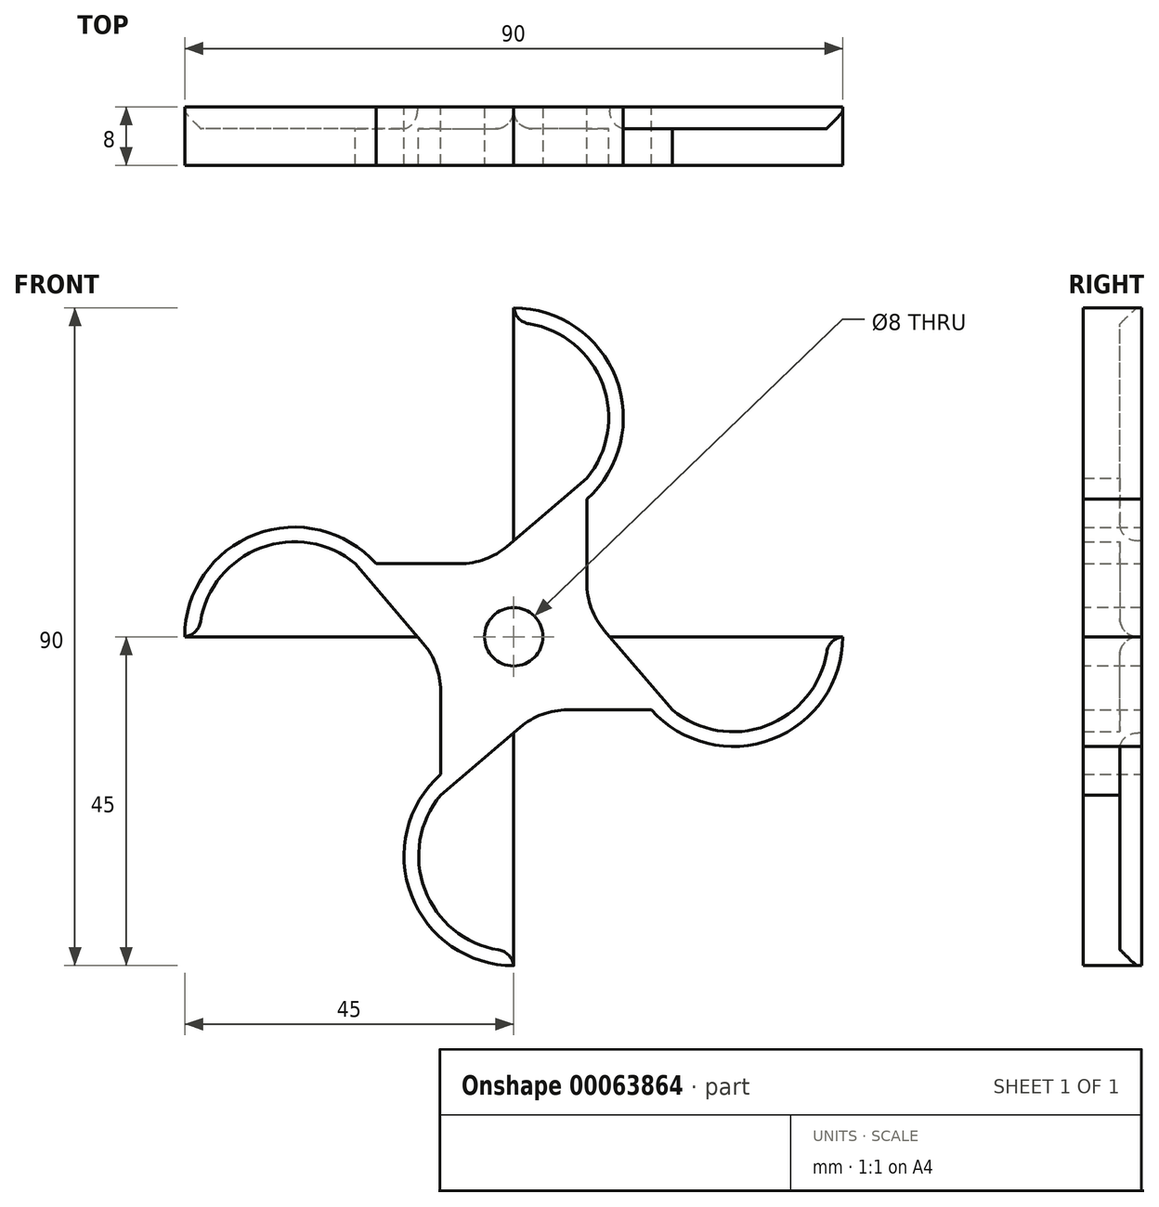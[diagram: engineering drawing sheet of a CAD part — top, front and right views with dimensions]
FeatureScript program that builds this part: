
annotation { "Feature Type Name" : "Feature", "Feature Type Description" : "" }
export const myFeature = defineFeature(function(context is Context, id is Id, definition is map)
    precondition{}
    {
        {
            var Q0;
            Q0=qCreatedBy(makeId("Front.planeOp"),FACE);
            var sketch = newSketch(context, id + "F0", { "sketchPlane" : qUnion([Q0])});
            skArc(sketch, "E0", {"start": v(10, 18.82) * mm, "mid": v(14.01, 35.35) * mm, "end": v(0, 45) * mm});
            skArc(sketch, "E1", {"start": v(10, 21.7) * mm, "mid": v(11.77, 35.52) * mm, "end": v(0, 43) * mm});
            skLineSegment(sketch, "E2", {"start": v(0, 13.15) * mm, "end": v(0, 10) * mm});
            skLineSegment(sketch, "E3", {"start": v(10, 7.38) * mm, "end": v(10, 18.82) * mm});
            skLineSegment(sketch, "E4", {"start": v(0, 43) * mm, "end": v(0, 45) * mm});
            skArc(sketch, "E5.1.1", {"start": v(-21.7, 10) * mm, "mid": v(-35.52, 11.77) * mm, "end": v(-43, 0) * mm});
            skLineSegment(sketch, "E5.1.2", {"start": v(-43, 0) * mm, "end": v(-45, 0) * mm});
            skArc(sketch, "E5.1.3", {"start": v(-18.82, 10) * mm, "mid": v(-35.35, 14.01) * mm, "end": v(-45, 0) * mm});
            skLineSegment(sketch, "E5.1.4", {"start": v(-7.38, 10) * mm, "end": v(-18.82, 10) * mm});
            skArc(sketch, "E5.2.1", {"start": v(-10, -21.7) * mm, "mid": v(-11.77, -35.52) * mm, "end": v(0, -43) * mm});
            skLineSegment(sketch, "E5.2.2", {"start": v(0, -43) * mm, "end": v(0, -45) * mm});
            skArc(sketch, "E5.2.3", {"start": v(-10, -18.82) * mm, "mid": v(-14.01, -35.35) * mm, "end": v(0, -45) * mm});
            skLineSegment(sketch, "E5.2.4", {"start": v(-10, -7.38) * mm, "end": v(-10, -18.82) * mm});
            skLineSegment(sketch, "E5.3.0", {"start": v(17, 0) * mm, "end": v(17, 0) * mm});
            skArc(sketch, "E5.3.1", {"start": v(21.7, -10) * mm, "mid": v(35.52, -11.77) * mm, "end": v(43, 0) * mm});
            skLineSegment(sketch, "E5.3.2", {"start": v(43, 0) * mm, "end": v(45, 0) * mm});
            skArc(sketch, "E5.3.3", {"start": v(18.82, -10) * mm, "mid": v(35.35, -14.01) * mm, "end": v(45, 0) * mm});
            skLineSegment(sketch, "E5.3.4", {"start": v(7.38, -10) * mm, "end": v(18.82, -10) * mm});
            skPoint(sketch, "E5.center", {"position": v(0, 0) * mm});
            skPoint(sketch, "E6.visualSharp", {"position": v(10, 0) * mm});
            skLineSegment(sketch, "E7", {"start": v(10, 21.7) * mm, "end": v(-0.88, 12.4) * mm});
            skPoint(sketch, "E8.orphan", {"position": v(0, 17) * mm});
            skPoint(sketch, "E9.newPointB", {"position": v(0, 10) * mm});
            skArc(sketch, "E9.filletArc", {"start": v(-7.38, 10) * mm, "mid": v(-3.92, 10.62) * mm, "end": v(-0.88, 12.4) * mm});
            skArc(sketch, "E10.1.0", {"start": v(-10, -7.38) * mm, "mid": v(-10.62, -3.92) * mm, "end": v(-12.4, -0.88) * mm});
            skLineSegment(sketch, "E10.1.1", {"start": v(-21.7, 10) * mm, "end": v(-12.4, -0.88) * mm});
            skArc(sketch, "E10.2.0", {"start": v(7.38, -10) * mm, "mid": v(3.92, -10.62) * mm, "end": v(0.88, -12.4) * mm});
            skLineSegment(sketch, "E10.2.1", {"start": v(-10, -21.7) * mm, "end": v(0.88, -12.4) * mm});
            skArc(sketch, "E10.3.0", {"start": v(10, 7.38) * mm, "mid": v(10.62, 3.92) * mm, "end": v(12.4, 0.88) * mm});
            skLineSegment(sketch, "E10.3.1", {"start": v(21.7, -10) * mm, "end": v(12.4, 0.88) * mm});
            skPoint(sketch, "E11.orphan", {"position": v(17, 0) * mm});
            skPoint(sketch, "E12.orphan", {"position": v(10, 7) * mm});
            skPoint(sketch, "E13.orphan", {"position": v(0, -17) * mm});
            skPoint(sketch, "E14.orphan", {"position": v(0, -10) * mm});
            skPoint(sketch, "E15.orphan", {"position": v(-10, 0) * mm});
            skPoint(sketch, "E16.orphan", {"position": v(-17, 0) * mm});
            skCircle(sketch, "E17", {"center": v(0, 0) * mm, "radius": 3.75 * mm});
            skSolve(sketch);
        }
        {
            var Q0;
            Q0=makeQuery(id+"F0.imprint","IMPRINT",FACE,{"disambiguationData":[TD([[makeQuery(id+"F0.imprint","IMPRINT",EDGE,{"derivedFrom":sQuery(id+"F0.wireOp",EDGE,"E0")}),1.0]])]});
            extrude(context, id + "F1", {"entities" : qUnion([Q0]), "depth" : 5 * mm});
        }
        {
            var Q0;
            Q0=makeQuery(id+"F1.opExtrude","CAP_FACE",FACE,{"disambiguationData":[OSD([sQuery(id+"F0.wireOp",EDGE,"E0"),sQuery(id+"F0.wireOp",EDGE,"E1"),sQuery(id+"F0.wireOp",EDGE,"E3"),sQuery(id+"F0.wireOp",EDGE,"E4"),sQuery(id+"F0.wireOp",EDGE,"E5.1.1"),sQuery(id+"F0.wireOp",EDGE,"E5.1.2"),sQuery(id+"F0.wireOp",EDGE,"E5.1.3"),sQuery(id+"F0.wireOp",EDGE,"E5.1.4"),sQuery(id+"F0.wireOp",EDGE,"E5.2.1"),sQuery(id+"F0.wireOp",EDGE,"E5.2.2"),sQuery(id+"F0.wireOp",EDGE,"E5.2.3"),sQuery(id+"F0.wireOp",EDGE,"E5.2.4"),sQuery(id+"F0.wireOp",EDGE,"E5.3.1"),sQuery(id+"F0.wireOp",EDGE,"E5.3.2"),sQuery(id+"F0.wireOp",EDGE,"E5.3.3"),sQuery(id+"F0.wireOp",EDGE,"E5.3.4"),sQuery(id+"F0.wireOp",EDGE,"E7"),sQuery(id+"F0.wireOp",EDGE,"E9.filletArc"),sQuery(id+"F0.wireOp",EDGE,"E10.1.0"),sQuery(id+"F0.wireOp",EDGE,"E10.1.1"),sQuery(id+"F0.wireOp",EDGE,"E10.2.0"),sQuery(id+"F0.wireOp",EDGE,"E10.2.1"),sQuery(id+"F0.wireOp",EDGE,"E10.3.0"),sQuery(id+"F0.wireOp",EDGE,"E10.3.1"),sQuery(id+"F0.wireOp",EDGE,"E17")])],"isStart":true});
            var sketch = newSketch(context, id + "F2", { "sketchPlane" : qUnion([Q0])});
            skArc(sketch, "E18", {"start": v(0, 45) * mm, "mid": v(-14.01, 35.35) * mm, "end": v(-10, 18.82) * mm});
            skPoint(sketch, "E18.first.point", {"position": v(-2.98, 44.7) * mm});
            skPoint(sketch, "E18.second.point", {"position": v(-12.28, 38.61) * mm});
            skPoint(sketch, "E18.third.point", {"position": v(-10.97, 19.77) * mm});
            skLineSegment(sketch, "E19", {"start": v(0, 9.88) * mm, "end": v(0, 45) * mm});
            skLineSegment(sketch, "E20", {"start": v(-10, 18.82) * mm, "end": v(-10, 7.38) * mm});
            skArc(sketch, "E21", {"start": v(-12.4, 0.88) * mm, "mid": v(-10.62, 3.92) * mm, "end": v(-10, 7.38) * mm});
            skPoint(sketch, "E21.first.point", {"position": v(-11.49, 2.13) * mm});
            skPoint(sketch, "E21.second.point", {"position": v(-11, 3.02) * mm});
            skPoint(sketch, "E21.third.point", {"position": v(-10.2, 5.4) * mm});
            skLineSegment(sketch, "E22", {"start": v(-13.15, 0) * mm, "end": v(-12.4, 0.88) * mm});
            skLineSegment(sketch, "E23", {"start": v(-13.15, 0) * mm, "end": v(-3.75, 0) * mm});
            skLineSegment(sketch, "E24", {"start": v(0, 3.75) * mm, "end": v(0, 9.88) * mm});
            skArc(sketch, "E25", {"start": v(0, 3.75) * mm, "mid": v(-2.65, 2.65) * mm, "end": v(-3.75, 0) * mm});
            skPoint(sketch, "E25.third.point", {"position": v(-2.3, 2.96) * mm});
            skArc(sketch, "E26.1.0", {"start": v(-3.75, 0) * mm, "mid": v(-2.65, -2.65) * mm, "end": v(0, -3.75) * mm});
            skLineSegment(sketch, "E26.1.1", {"start": v(0, -13.15) * mm, "end": v(-0.88, -12.4) * mm});
            skArc(sketch, "E26.1.2", {"start": v(-0.88, -12.4) * mm, "mid": v(-3.92, -10.62) * mm, "end": v(-7.38, -10) * mm});
            skLineSegment(sketch, "E26.1.3", {"start": v(-18.82, -10) * mm, "end": v(-7.38, -10) * mm});
            skArc(sketch, "E26.1.4", {"start": v(-45, 0) * mm, "mid": v(-35.35, -14.01) * mm, "end": v(-18.82, -10) * mm});
            skLineSegment(sketch, "E26.1.5", {"start": v(-9.88, 0) * mm, "end": v(-45, 0) * mm});
            skLineSegment(sketch, "E26.1.6", {"start": v(-3.75, 0) * mm, "end": v(-9.88, 0) * mm});
            skArc(sketch, "E26.2.0", {"start": v(0, -3.75) * mm, "mid": v(2.65, -2.65) * mm, "end": v(3.75, 0) * mm});
            skLineSegment(sketch, "E26.2.1", {"start": v(13.15, 0) * mm, "end": v(12.4, -0.88) * mm});
            skArc(sketch, "E26.2.2", {"start": v(12.4, -0.88) * mm, "mid": v(10.62, -3.92) * mm, "end": v(10, -7.38) * mm});
            skLineSegment(sketch, "E26.2.3", {"start": v(10, -18.82) * mm, "end": v(10, -7.38) * mm});
            skArc(sketch, "E26.2.4", {"start": v(0, -45) * mm, "mid": v(14.01, -35.35) * mm, "end": v(10, -18.82) * mm});
            skLineSegment(sketch, "E26.2.5", {"start": v(0, -9.88) * mm, "end": v(0, -45) * mm});
            skLineSegment(sketch, "E26.2.6", {"start": v(0, -3.75) * mm, "end": v(0, -9.88) * mm});
            skArc(sketch, "E26.3.0", {"start": v(3.75, 0) * mm, "mid": v(2.65, 2.65) * mm, "end": v(0, 3.75) * mm});
            skLineSegment(sketch, "E26.3.1", {"start": v(0, 13.15) * mm, "end": v(0.88, 12.4) * mm});
            skArc(sketch, "E26.3.2", {"start": v(0.88, 12.4) * mm, "mid": v(3.92, 10.62) * mm, "end": v(7.38, 10) * mm});
            skLineSegment(sketch, "E26.3.3", {"start": v(18.82, 10) * mm, "end": v(7.38, 10) * mm});
            skArc(sketch, "E26.3.4", {"start": v(45, 0) * mm, "mid": v(35.35, 14.01) * mm, "end": v(18.82, 10) * mm});
            skLineSegment(sketch, "E26.3.5", {"start": v(9.88, 0) * mm, "end": v(45, 0) * mm});
            skLineSegment(sketch, "E26.3.6", {"start": v(3.75, 0) * mm, "end": v(9.88, 0) * mm});
            skSolve(sketch);
        }
        {
            var Q0;
            {var subQ1=makeQuery(id+"F1.opExtrude","CAP_EDGE",EDGE,{"disambiguationData":[OSD([sQuery(id+"F0.wireOp",EDGE,"E1")])],"isStart":true});Q0=makeQuery(id+"F2.imprint","IMPRINT",FACE,{"disambiguationData":[TD([[makeQuery(id+"F2.imprint","IMPRINT",EDGE,{"derivedFrom":subQ1}),-1.0]])]});}
            var Q1;
            {var subQ6=sQuery(id+"F2.wireOp",EDGE,"E18");Q1=makeQuery(id+"F2.imprint","IMPRINT",FACE,{"disambiguationData":[TD([[makeQuery(id+"F2.imprint","IMPRINT",EDGE,{"derivedFrom":subQ6}),-1.0]])]});}
            var Q2;
            {var subQ4=sQuery(id+"F2.wireOp",EDGE,"E24");Q2=makeQuery(id+"F2.imprint","IMPRINT",FACE,{"disambiguationData":[TD([[makeQuery(id+"F2.imprint","IMPRINT",EDGE,{"derivedFrom":subQ4}),-1.0]])]});}
            var Q3;
            {var subQ1=makeQuery(id+"F1.opExtrude","CAP_EDGE",EDGE,{"disambiguationData":[OSD([sQuery(id+"F0.wireOp",EDGE,"E5.1.1")])],"isStart":true});Q3=makeQuery(id+"F2.imprint","IMPRINT",FACE,{"disambiguationData":[TD([[makeQuery(id+"F2.imprint","IMPRINT",EDGE,{"derivedFrom":subQ1}),-1.0]])]});}
            var Q4;
            Q4=makeQuery(id+"F2.imprint","IMPRINT",FACE,{"disambiguationData":[TD([[makeQuery(id+"F2.imprint","IMPRINT",EDGE,{"derivedFrom":sQuery(id+"F2.wireOp",EDGE,"E26.2.0")}),1.0]])]});
            var Q5;
            {var subQ1=makeQuery(id+"F1.opExtrude","CAP_EDGE",EDGE,{"disambiguationData":[OSD([sQuery(id+"F0.wireOp",EDGE,"E5.2.1")])],"isStart":true});Q5=makeQuery(id+"F2.imprint","IMPRINT",FACE,{"disambiguationData":[TD([[makeQuery(id+"F2.imprint","IMPRINT",EDGE,{"derivedFrom":subQ1}),-1.0]])]});}
            var Q6;
            Q6=makeQuery(id+"F2.imprint","IMPRINT",FACE,{"disambiguationData":[TD([[makeQuery(id+"F2.imprint","IMPRINT",EDGE,{"derivedFrom":sQuery(id+"F2.wireOp",EDGE,"E26.1.0")}),1.0]])]});
            var Q7;
            {var subQ1=makeQuery(id+"F1.opExtrude","CAP_EDGE",EDGE,{"disambiguationData":[OSD([sQuery(id+"F0.wireOp",EDGE,"E5.3.1")])],"isStart":true});Q7=makeQuery(id+"F2.imprint","IMPRINT",FACE,{"disambiguationData":[TD([[makeQuery(id+"F2.imprint","IMPRINT",EDGE,{"derivedFrom":subQ1}),-1.0]])]});}
            extrude(context, id + "F3", {"entities" : qUnion([Q0, Q1, Q2, Q3, Q4, Q5, Q6, Q7]), "operationType" : NewBodyOperationType.ADD, "depth" : 3 * mm});
        }
        {
            var Q0;
            Q0=makeQuery(id+"F3.opExtrude","CAP_EDGE",EDGE,{"disambiguationData":[OSD([sQuery(id+"F2.wireOp",EDGE,"E19")])],"isStart":true});
            var Q1;
            Q1=makeQuery(id+"F3.opExtrude","CAP_EDGE",EDGE,{"disambiguationData":[OSD([sQuery(id+"F2.wireOp",EDGE,"E26.2.5")])],"isStart":true});
            var Q2;
            Q2=makeQuery(id+"F3.opExtrude","CAP_EDGE",EDGE,{"disambiguationData":[OSD([sQuery(id+"F2.wireOp",EDGE,"E26.1.5")])],"isStart":true});
            var Q3;
            Q3=makeQuery(id+"F3.opExtrude","CAP_EDGE",EDGE,{"disambiguationData":[OSD([sQuery(id+"F2.wireOp",EDGE,"E26.3.5")])],"isStart":true});
            fillet(context, id + "F4", {"entities" : qUnion([Q0, Q1, Q2, Q3]), "radius" : 2.5 * mm, "tangentPropagation" : true, "allowEdgeOverflow" : false});
        }
        {
            var Q0;
            Q0=makeQuery(id+"F1.opExtrude","SWEPT_EDGE",EDGE,{"disambiguationData":[OSD([sQuery(id+"F0.wireOp",EDGE,"E5.2.1"),sQuery(id+"F0.wireOp",EDGE,"E5.2.2")])]});
            var Q1;
            Q1=makeQuery(id+"F1.opExtrude","SWEPT_EDGE",EDGE,{"disambiguationData":[OSD([sQuery(id+"F0.wireOp",EDGE,"E5.3.1"),sQuery(id+"F0.wireOp",EDGE,"E5.3.2")])]});
            var Q2;
            Q2=makeQuery(id+"F1.opExtrude","SWEPT_EDGE",EDGE,{"disambiguationData":[OSD([sQuery(id+"F0.wireOp",EDGE,"E1"),sQuery(id+"F0.wireOp",EDGE,"E4")])]});
            var Q3;
            Q3=makeQuery(id+"F1.opExtrude","SWEPT_EDGE",EDGE,{"disambiguationData":[OSD([sQuery(id+"F0.wireOp",EDGE,"E5.1.1"),sQuery(id+"F0.wireOp",EDGE,"E5.1.2")])]});
            fillet(context, id + "F5", {"entities" : qUnion([Q0, Q1, Q2, Q3]), "radius" : 2.5 * mm, "tangentPropagation" : true, "allowEdgeOverflow" : false});
        }
        {
            var Q0;
            Q0=makeQuery(id+"F1.opExtrude","CAP_FACE",FACE,{"disambiguationData":[OSD([sQuery(id+"F0.wireOp",EDGE,"E0"),sQuery(id+"F0.wireOp",EDGE,"E1"),sQuery(id+"F0.wireOp",EDGE,"E3"),sQuery(id+"F0.wireOp",EDGE,"E4"),sQuery(id+"F0.wireOp",EDGE,"E5.1.1"),sQuery(id+"F0.wireOp",EDGE,"E5.1.2"),sQuery(id+"F0.wireOp",EDGE,"E5.1.3"),sQuery(id+"F0.wireOp",EDGE,"E5.1.4"),sQuery(id+"F0.wireOp",EDGE,"E5.2.1"),sQuery(id+"F0.wireOp",EDGE,"E5.2.2"),sQuery(id+"F0.wireOp",EDGE,"E5.2.3"),sQuery(id+"F0.wireOp",EDGE,"E5.2.4"),sQuery(id+"F0.wireOp",EDGE,"E5.3.1"),sQuery(id+"F0.wireOp",EDGE,"E5.3.2"),sQuery(id+"F0.wireOp",EDGE,"E5.3.3"),sQuery(id+"F0.wireOp",EDGE,"E5.3.4"),sQuery(id+"F0.wireOp",EDGE,"E7"),sQuery(id+"F0.wireOp",EDGE,"E9.filletArc"),sQuery(id+"F0.wireOp",EDGE,"E10.1.0"),sQuery(id+"F0.wireOp",EDGE,"E10.1.1"),sQuery(id+"F0.wireOp",EDGE,"E10.2.0"),sQuery(id+"F0.wireOp",EDGE,"E10.2.1"),sQuery(id+"F0.wireOp",EDGE,"E10.3.0"),sQuery(id+"F0.wireOp",EDGE,"E10.3.1"),sQuery(id+"F0.wireOp",EDGE,"E17")])],"isStart":false});
            var sketch = newSketch(context, id + "F6", { "sketchPlane" : qUnion([Q0])});
            skCircle(sketch, "E27", {"center": v(0, 0) * mm, "radius": 45 * mm});
            skSolve(sketch);
        }
        {
            var Q0;
            Q0=makeQuery(id+"F6.imprint","IMPRINT",FACE,{"disambiguationData":[TD([[makeQuery(id+"F6.imprint","IMPRINT",EDGE,{"derivedFrom":makeQuery(id+"F1.opExtrude","CAP_EDGE",EDGE,{"disambiguationData":[OSD([sQuery(id+"F0.wireOp",EDGE,"E17")])],"isStart":false})}),1.0]])]});
            var sketch = newSketch(context, id + "F7", { "sketchPlane" : qUnion([Q0])});
            skCircle(sketch, "E28", {"center": v(0, 0) * mm, "radius": 4 * mm});
            skSolve(sketch);
        }
        {
            var Q0;
            Q0 = qSketchRegion(id + "F7", true);
            extrude(context, id + "F8", {"entities" : qUnion([Q0]), "operationType" : NewBodyOperationType.REMOVE, "endBound" : BoundingType.THROUGH_ALL, "oppositeDirection" : true, "depth" : 25 * mm});
        }
    });
